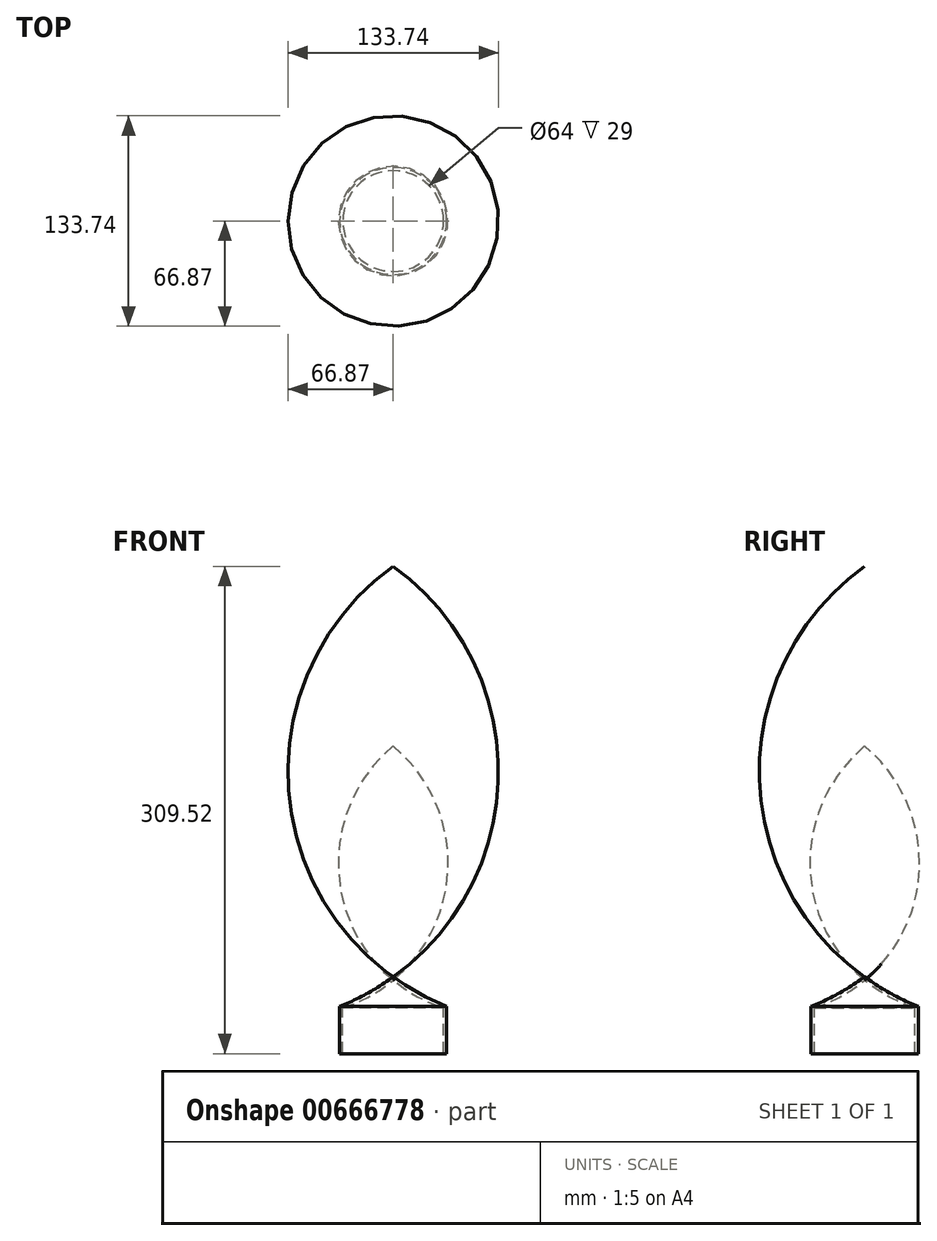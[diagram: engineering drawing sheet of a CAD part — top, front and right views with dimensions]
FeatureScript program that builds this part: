
annotation { "Feature Type Name" : "Feature", "Feature Type Description" : "" }
export const myFeature = defineFeature(function(context is Context, id is Id, definition is map)
    precondition{}
    {
        {
            var Q0;
            Q0=qCreatedBy(makeId("Right.planeOp"),FACE);
            var sketch = newSketch(context, id + "F0", { "sketchPlane" : qUnion([Q0])});
            skLineSegment(sketch, "E0", {"start": v(-32, 0) * mm, "end": v(-32, 29) * mm});
            skLineSegment(sketch, "E1", {"start": v(0, 46.64) * mm, "end": v(0, 0) * mm, "construction": true});
            skLineSegment(sketch, "E2.0", {"start": v(-34, 0) * mm, "end": v(-34, 30) * mm});
            skLineSegment(sketch, "E3", {"start": v(0, 48.67) * mm, "end": v(0, 46.64) * mm});
            skLineSegment(sketch, "E4", {"start": v(-32, 0) * mm, "end": v(-34, 0) * mm});
            skArc(sketch, "E5", {"start": v(-32, 29) * mm, "mid": v(-15.16, 36.3) * mm, "end": v(0, 46.64) * mm});
            skArc(sketch, "E6", {"start": v(-34, 30) * mm, "mid": v(-16.43, 38.3) * mm, "end": v(0, 48.67) * mm});
            skSolve(sketch);
        }
        {
            var Q0;
            Q0 = qSketchRegion(id + "F0", true);
            var Q1;
            Q1=sQuery(id+"F0.wireOp",EDGE,"E1");
            revolve(context, id + "F1", {"entities" : qUnion([Q0]), "axis" : qUnion([Q1]), "revolveType" : RevolveType.FULL});
        }
    });
